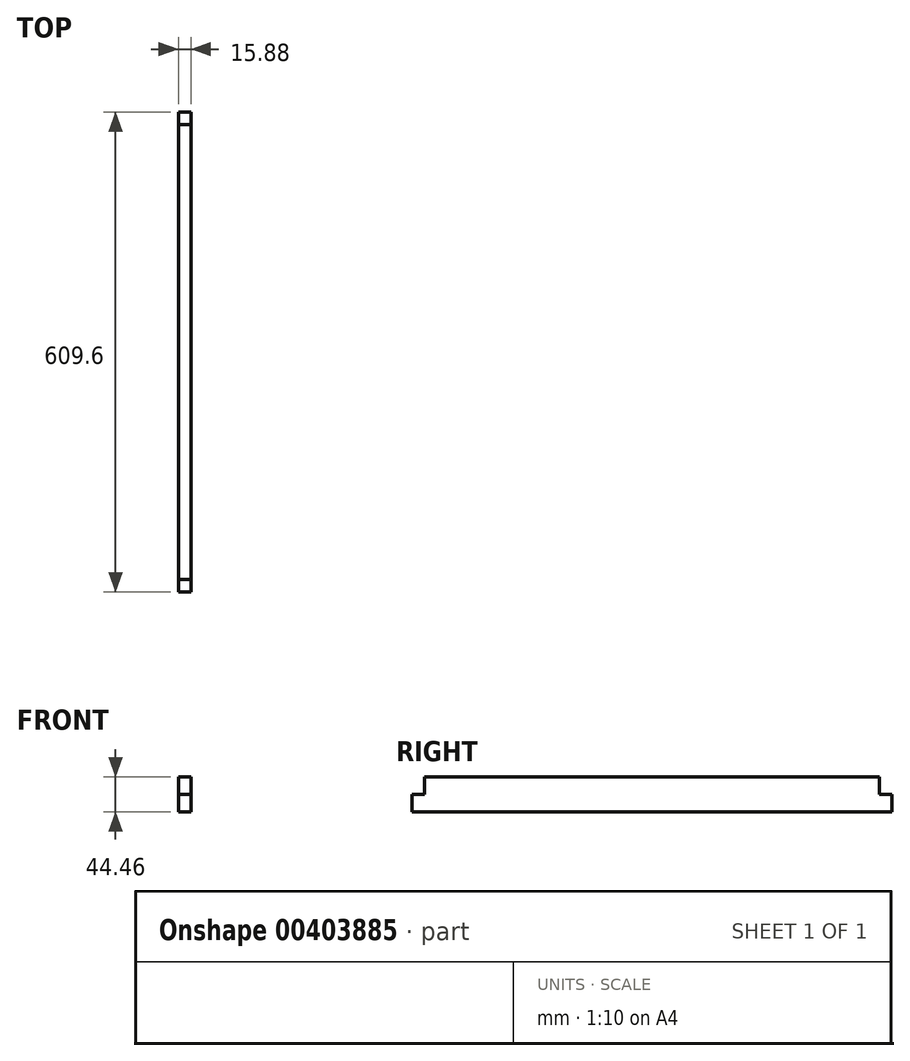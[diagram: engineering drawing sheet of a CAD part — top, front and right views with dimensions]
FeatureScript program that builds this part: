
annotation { "Feature Type Name" : "Feature", "Feature Type Description" : "" }
export const myFeature = defineFeature(function(context is Context, id is Id, definition is map)
    precondition{}
    {
        {
            var Q0;
            Q0=qCreatedBy(makeId("Right.planeOp"),FACE);
            var sketch = newSketch(context, id + "F0", { "sketchPlane" : qUnion([Q0])});
            skLineSegment(sketch, "E0.bottom", {"start": v(304.8, -22.23) * mm, "end": v(-304.8, -22.23) * mm});
            skLineSegment(sketch, "E0.top", {"start": v(304.8, 22.23) * mm, "end": v(-304.8, 22.22) * mm});
            skLineSegment(sketch, "E0.left", {"start": v(304.8, -22.23) * mm, "end": v(304.8, 22.23) * mm});
            skLineSegment(sketch, "E0.right", {"start": v(-304.8, -22.23) * mm, "end": v(-304.8, 22.22) * mm});
            skPoint(sketch, "E0.middle", {"position": v(0, 0) * mm});
            skSolve(sketch);
        }
        {
            var Q0;
            Q0 = qSketchRegion(id + "F0", true);
            extrude(context, id + "F1", {"entities" : qUnion([Q0]), "depth" : 15.88 * mm});
        }
        {
            var Q0;
            Q0=makeQuery(id+"F1.opExtrude","CAP_FACE",FACE,{"disambiguationData":[OSD([sQuery(id+"F0.wireOp",EDGE,"E0.bottom"),sQuery(id+"F0.wireOp",EDGE,"E0.top"),sQuery(id+"F0.wireOp",EDGE,"E0.left"),sQuery(id+"F0.wireOp",EDGE,"E0.right")])],"isStart":false});
            var sketch = newSketch(context, id + "F2", { "sketchPlane" : qUnion([Q0])});
            skLineSegment(sketch, "E1.bottom", {"start": v(-304.8, 22.22) * mm, "end": v(-288.93, 22.22) * mm});
            skLineSegment(sketch, "E1.top", {"start": v(-304.8, 0) * mm, "end": v(-288.93, 0) * mm});
            skLineSegment(sketch, "E1.left", {"start": v(-304.8, 22.22) * mm, "end": v(-304.8, 0) * mm});
            skLineSegment(sketch, "E1.right", {"start": v(-288.93, 22.22) * mm, "end": v(-288.93, 0) * mm});
            skLineSegment(sketch, "E2.MirrorCS", {"start": v(288.93, 22.22) * mm, "end": v(288.93, 0) * mm});
            skLineSegment(sketch, "E3.MirrorCS", {"start": v(304.8, 22.22) * mm, "end": v(304.8, 0) * mm});
            skLineSegment(sketch, "E4.MirrorCS", {"start": v(304.8, 22.22) * mm, "end": v(288.93, 22.22) * mm});
            skLineSegment(sketch, "E5.MirrorCS", {"start": v(304.8, 0) * mm, "end": v(288.93, 0) * mm});
            skSolve(sketch);
        }
        {
            var Q0;
            Q0 = qSketchRegion(id + "F2", true);
            extrude(context, id + "F3", {"entities" : qUnion([Q0]), "operationType" : NewBodyOperationType.REMOVE, "endBound" : BoundingType.THROUGH_ALL, "oppositeDirection" : true, "depth" : 25.4 * mm});
        }
    });
